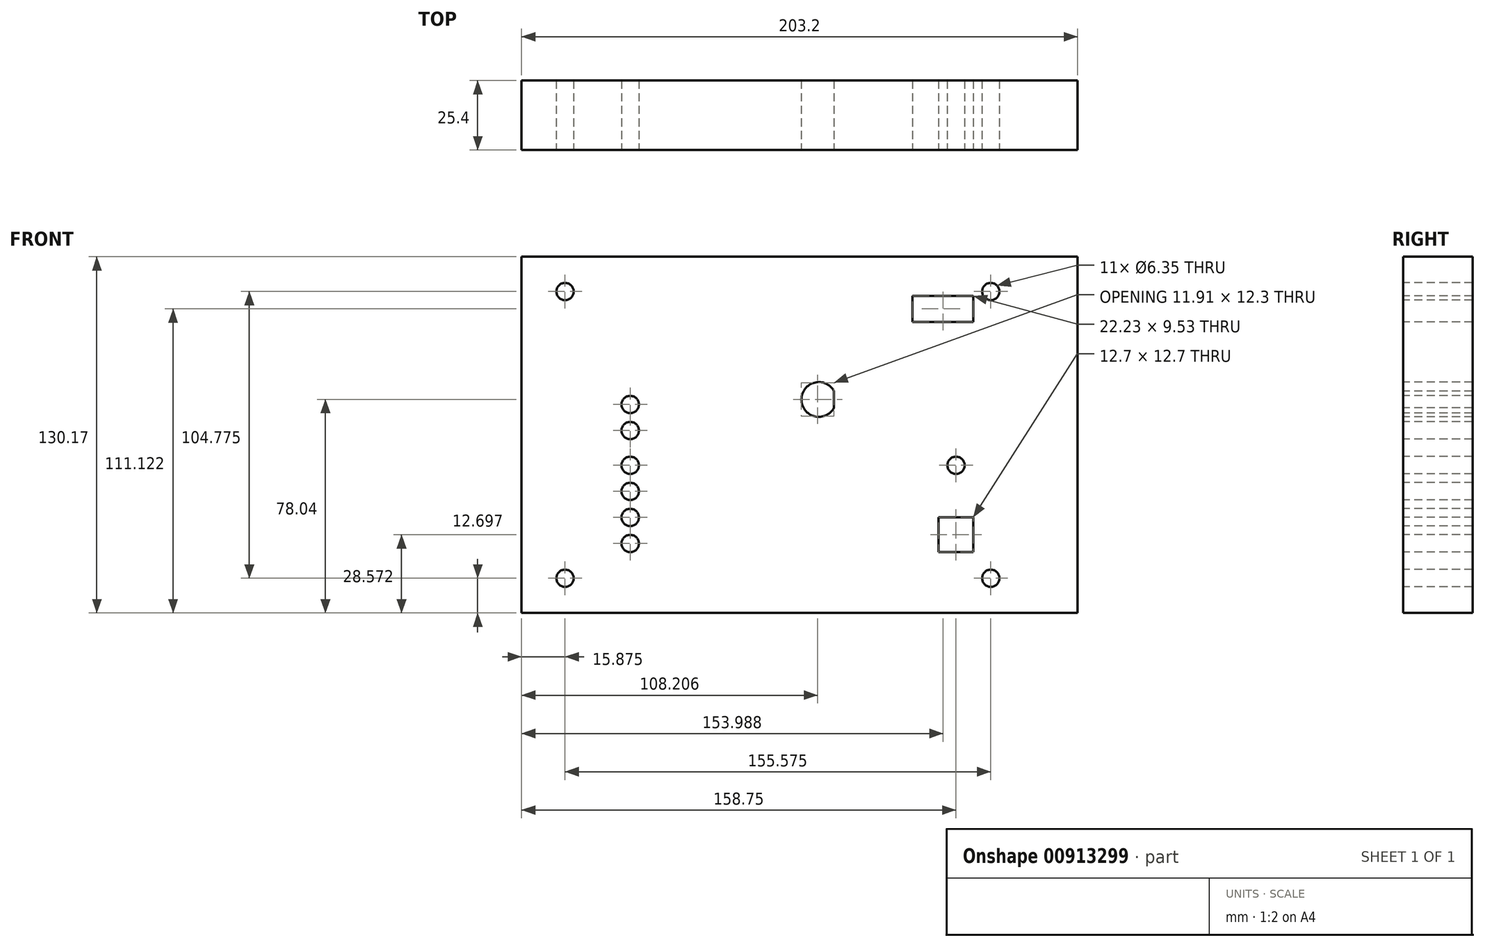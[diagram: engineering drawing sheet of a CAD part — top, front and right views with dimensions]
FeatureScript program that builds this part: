
annotation { "Feature Type Name" : "Feature", "Feature Type Description" : "" }
export const myFeature = defineFeature(function(context is Context, id is Id, definition is map)
    precondition{}
    {
        {
            var Q0;
            Q0=qCreatedBy(makeId("Front.planeOp"),FACE);
            var sketch = newSketch(context, id + "F0", { "sketchPlane" : qUnion([Q0])});
            skCircle(sketch, "E0", {"center": v(-92.08, 39.43) * mm, "radius": 3.18 * mm});
            skLineSegment(sketch, "E1.bottom", {"start": v(-107.95, 52.13) * mm, "end": v(95.25, 52.13) * mm});
            skLineSegment(sketch, "E1.top", {"start": v(-107.95, -78.04) * mm, "end": v(95.25, -78.04) * mm});
            skLineSegment(sketch, "E1.left", {"start": v(-107.95, 52.13) * mm, "end": v(-107.95, -78.04) * mm});
            skLineSegment(sketch, "E1.right", {"start": v(95.25, 52.13) * mm, "end": v(95.25, -78.04) * mm});
            skCircle(sketch, "E2", {"center": v(-92.07, -65.34) * mm, "radius": 3.18 * mm});
            skCircle(sketch, "E3", {"center": v(63.5, -65.34) * mm, "radius": 3.18 * mm});
            skCircle(sketch, "E4", {"center": v(63.5, 39.43) * mm, "radius": 3.18 * mm});
            skLineSegment(sketch, "E5.bottom", {"start": v(57.15, -55.82) * mm, "end": v(44.45, -55.82) * mm});
            skLineSegment(sketch, "E5.top", {"start": v(57.15, -43.12) * mm, "end": v(44.45, -43.12) * mm});
            skLineSegment(sketch, "E5.left", {"start": v(57.15, -55.82) * mm, "end": v(57.15, -43.12) * mm});
            skLineSegment(sketch, "E5.right", {"start": v(44.45, -55.82) * mm, "end": v(44.45, -43.12) * mm});
            skCircle(sketch, "E6", {"center": v(50.8, -24.07) * mm, "radius": 3.18 * mm});
            skLineSegment(sketch, "E7.bottom", {"start": v(34.92, 37.84) * mm, "end": v(57.15, 37.84) * mm});
            skLineSegment(sketch, "E7.top", {"start": v(34.92, 28.32) * mm, "end": v(57.15, 28.32) * mm});
            skLineSegment(sketch, "E7.left", {"start": v(34.92, 37.84) * mm, "end": v(34.92, 28.32) * mm});
            skLineSegment(sketch, "E7.right", {"start": v(57.15, 37.84) * mm, "end": v(57.15, 28.32) * mm});
            skCircle(sketch, "E8", {"center": v(-68.26, -52.64) * mm, "radius": 3.18 * mm});
            skCircle(sketch, "E9", {"center": v(-68.26, -43.12) * mm, "radius": 3.18 * mm});
            skCircle(sketch, "E10", {"center": v(-68.26, -24.07) * mm, "radius": 3.18 * mm});
            skCircle(sketch, "E11", {"center": v(-68.26, -33.6) * mm, "radius": 3.18 * mm});
            skCircle(sketch, "E12", {"center": v(-68.26, -11.37) * mm, "radius": 3.18 * mm});
            skCircle(sketch, "E13", {"center": v(-68.26, -1.84) * mm, "radius": 3.18 * mm});
            skArc(sketch, "E14", {"start": v(6.2, 3.07) * mm, "mid": v(-5.7, 0) * mm, "end": v(6.2, -3.07) * mm});
            skPoint(sketch, "E15.start.orphan", {"position": v(-5.7, 0) * mm});
            skLineSegment(sketch, "E16", {"start": v(6.2, -3.07) * mm, "end": v(6.2, 3.07) * mm});
            skSolve(sketch);
        }
        {
            var Q0;
            Q0 = qSketchRegion(id + "F0", true);
            extrude(context, id + "F1", {"entities" : qUnion([Q0]), "depth" : -25.4 * mm, "offsetDistance" : 25.4 * mm});
        }
    });
